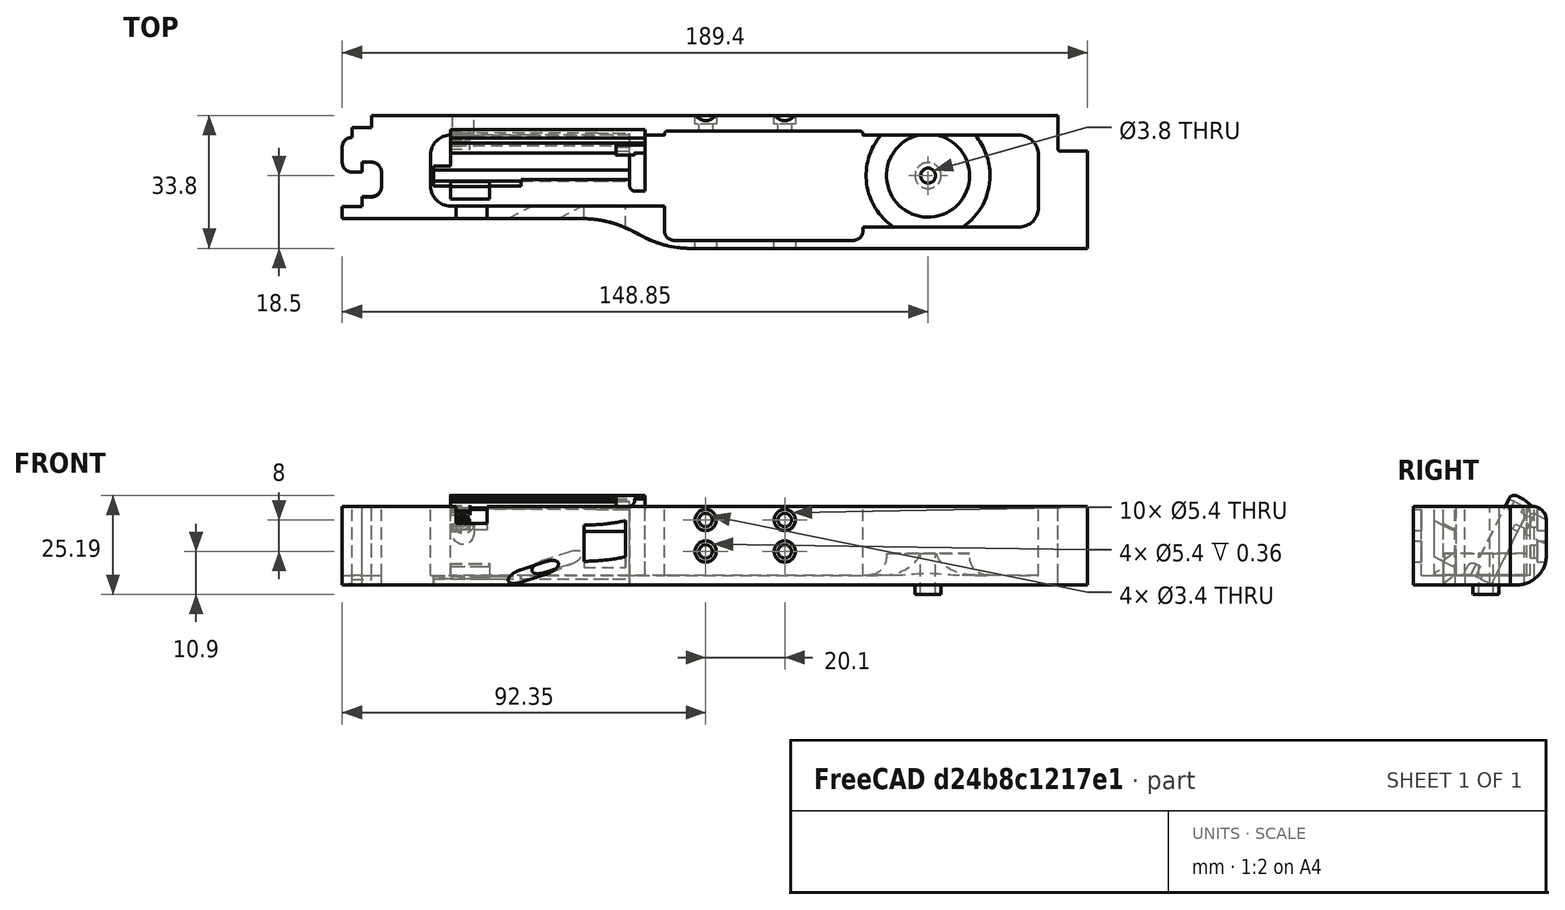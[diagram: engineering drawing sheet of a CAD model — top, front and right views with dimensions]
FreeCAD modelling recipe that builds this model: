
FCSTD DOCUMENT  (FreeCAD 0.19R0.19.2)
Label: v0_998
License: All rights reserved
LicenseURL: http://en.wikipedia.org/wiki/All_rights_reserved
objects: Sketcher::SketchObject×39, Part::Extrusion×31, Part::MultiFuse×19, Part::Cut×15, Part::Box×14, Part::Fillet×11, App::MeasureDistance×4, Part::Cylinder×4, Part::Revolution×1, Mesh::Feature×1
note: 134 computed .brp shape members not serialized (recipe doc carries the construction recipe); baked Part::Feature solids carry a one-line shape summary decoded from their .brp

FEATURE [Sketcher::SketchObject] Sketch
  FullyConstrained = true
  sketch-geometry (36):
    g0: LineSegment StartX=0 StartY=0 StartZ=0 EndX=154.4 EndY=0 EndZ=0
    g1: LineSegment StartX=154.4 StartY=0 StartZ=0 EndX=154.4 EndY=-7.6 EndZ=0
    g2: LineSegment StartX=32.5209 StartY=-26.2 StartZ=0 EndX=-7.5 EndY=-26.2 EndZ=0
    g3-g7: Circle x5 (B-spline internal-alignment scaffolding for g8; pole/knot coordinates omitted)
    g8: BSplineCurve PolesCount=5 KnotsCount=3 Degree=3 IsPeriodic=0
    g9: GeomPoint X=61.85 Y=-33.8 Z=0
    g10: GeomPoint X=47.185 Y=-29.9 Z=0
    g11: GeomPoint X=32.5209 Y=-26.2 Z=0
    g12: Circle CenterX=121.35 CenterY=-14.3 CenterZ=0 NormalX=0 NormalY=0 NormalZ=1 AngleXU=0 Radius=3.25
    g13: LineSegment StartX=-7.5 StartY=-26.2 StartZ=0 EndX=-27.5 EndY=-26.2 EndZ=0
    g14: LineSegment StartX=-20 StartY=0 StartZ=0 EndX=0 EndY=0 EndZ=0
    g15: LineSegment StartX=-25 StartY=-3.1 StartZ=0 EndX=-20 EndY=-3.1 EndZ=0
    g16: LineSegment StartX=-25 StartY=-3.1 StartZ=0 EndX=-25 EndY=-5.6 EndZ=0
    g17: LineSegment StartX=-27.5 StartY=-8.1 StartZ=0 EndX=-27.5 EndY=-11.85 EndZ=0
    g18: ArcOfCircle CenterX=-25 CenterY=-8.1 CenterZ=0 NormalX=0 NormalY=0 NormalZ=1 AngleXU=0 Radius=2.5 StartAngle=1.5708 EndAngle=3.14159
    g19: LineSegment StartX=-25 StartY=-14.35 StartZ=0 EndX=-22.5 EndY=-14.35 EndZ=0
    g20: ArcOfCircle CenterX=-25 CenterY=-11.85 CenterZ=0 NormalX=0 NormalY=0 NormalZ=1 AngleXU=0 Radius=2.5 StartAngle=3.14159 EndAngle=4.71239
    g21: LineSegment StartX=-22.5 StartY=-14.35 StartZ=0 EndX=-22.5 EndY=-11.85 EndZ=0
    g22: LineSegment StartX=-22.5 StartY=-11.85 StartZ=0 EndX=-20 EndY=-11.85 EndZ=0
    g23: ArcOfCircle CenterX=-20 CenterY=-14.35 CenterZ=0 NormalX=0 NormalY=0 NormalZ=1 AngleXU=0 Radius=2.5 StartAngle=8e-16 EndAngle=1.5708
    g24: LineSegment StartX=-17.5 StartY=-14.35 StartZ=0 EndX=-17.5 EndY=-18.1 EndZ=0
    g25: ArcOfCircle CenterX=-20 CenterY=-18.1 CenterZ=0 NormalX=0 NormalY=0 NormalZ=1 AngleXU=0 Radius=2.5 StartAngle=4.71239 EndAngle=6.28319
    g26: LineSegment StartX=-22.5 StartY=-20.6 StartZ=0 EndX=-20 EndY=-20.6 EndZ=0
    g27: LineSegment StartX=-22.5 StartY=-20.6 StartZ=0 EndX=-22.5 EndY=-23.1 EndZ=0
    g28: LineSegment StartX=-27.5 StartY=-23.1 StartZ=0 EndX=-22.5 EndY=-23.1 EndZ=0
    g29: LineSegment StartX=-20 StartY=-3.1 StartZ=0 EndX=-20 EndY=0 EndZ=0
    g30: LineSegment StartX=-27.5 StartY=-23.1 StartZ=0 EndX=-27.5 EndY=-26.2 EndZ=0
    g31: LineSegment StartX=154.4 StartY=-7.6 StartZ=0 EndX=154.4 EndY=-8.6 EndZ=0
    g32: ArcOfCircle CenterX=154.9 CenterY=-8.6 CenterZ=0 NormalX=0 NormalY=0 NormalZ=1 AngleXU=0 Radius=0.5 StartAngle=3.14159 EndAngle=4.71239
    g33: LineSegment StartX=154.9 StartY=-9.1 StartZ=0 EndX=161.9 EndY=-9.1 EndZ=0
    g34: LineSegment StartX=161.9 StartY=-9.1 StartZ=0 EndX=161.9 EndY=-33.8 EndZ=0
    g35: LineSegment StartX=161.9 StartY=-33.8 StartZ=0 EndX=61.85 EndY=-33.8 EndZ=0
  constraints (72):
    c: PointOnObject(g0,g-2)
    c: Horizontal(g0)
    c: Distance(g0) = 154.4
    c: DistanceY(g-1,g0) = 0
    c: Vertical(g1)
    c: Distance(g1) = 7.6
    c: Coincident(g1,g0)
    c: Horizontal(g2)
    c: Block(g2)
    c: Weight(g3) = 1
    c: Coincident(g8,g2)
    c: InternalAlignment(g3-g7 -> g8) x5
    c: InternalAlignment(g9,g8)
    c: InternalAlignment(g10,g8)
    c: InternalAlignment(g11,g8)
    c: Block(g12)
    c: Coincident(g13,g2)
    c: Horizontal(g13)
    c: Distance(g13) = 20
    c: Horizontal(g14)
    c: Distance(g14) = 20
    c: Coincident(g14,g0)
    c: Horizontal(g15)
    c: Vertical(g16)
    c: Coincident(g16,g15)
    c: Vertical(g17)
    c: Coincident(g18,g16)
    c: Block(g18)
    c: Coincident(g17,g18)
    c: Horizontal(g19)
    c: Coincident(g20,g17)
    c: Block(g20)
    c: Block(g19)
    c: Vertical(g21)
    c: Coincident(g21,g19)
    c: Horizontal(g22)
    c: Coincident(g22,g21)
    c: Coincident(g23,g22)
    c: Vertical(g24)
    c: Block(g23)
    c: Coincident(g24,g23)
    c: Coincident(g25,g24)
    c: Block(g25)
    c: Horizontal(g26)
    c: Coincident(g26,g25)
    c: Vertical(g27)
    c: Coincident(g27,g26)
    c: Horizontal(g28)
    c: Coincident(g28,g27)
    c: Block(g15)
    c: Block(g28)
    c: Coincident(g29,g15)
    c: Coincident(g29,g14)
    c: Vertical(g29)
    c: Coincident(g30,g28)
    c: Coincident(g30,g13)
    c: Vertical(g30)
    c: Vertical(g31)
    c: Distance(g31) = 1
    c: Coincident(g31,g1)
    c: Coincident(g32,g31)
    c: Block(g32)
    c: Coincident(g33,g32)
    c: Horizontal(g33)
    c: Coincident(g34,g33)
    c: Vertical(g34)
    c: Block(g34)
    c: Coincident(g35,g34)
    c: Horizontal(g35)
    c: Block(g35)
    c: Coincident(g8,g35)
    c: Block(g8)
FEATURE [Part::Extrusion] Extrude  label="mainBodyBaseExtrude"
  Base = -> Sketch
  Dir = (0,0,1)
  DirMode = 2
  FaceMakerClass = Part::FaceMakerBullseye
  LengthFwd = 2.4
  LengthRev = 0
  Solid = true
  Symmetric = false
FEATURE [Sketcher::SketchObject] Sketch001
  FullyConstrained = true
  sketch-geometry (75):
    g0: ArcOfCircle CenterX=144.4 CenterY=-10 CenterZ=0 NormalX=0 NormalY=0 NormalZ=1 AngleXU=0 Radius=5 StartAngle=4.345e-13 EndAngle=1.5708
    g1: LineSegment StartX=32.5209 StartY=-26.2 StartZ=0 EndX=-7.49911 EndY=-26.2 EndZ=0
    g2: LineSegment StartX=0 StartY=0 StartZ=0 EndX=154.4 EndY=0 EndZ=0
    g3-g7: Circle x5 (B-spline internal-alignment scaffolding for g8; pole/knot coordinates omitted)
    g8: BSplineCurve PolesCount=5 KnotsCount=3 Degree=3 IsPeriodic=0
    g9: GeomPoint X=61.85 Y=-33.8 Z=0
    g10: GeomPoint X=47.1857 Y=-29.9 Z=0
    g11: GeomPoint X=32.5209 Y=-26.2 Z=0
    g12: LineSegment StartX=154.4 StartY=0 StartZ=0 EndX=154.4 EndY=-7.6 EndZ=0
    g13: LineSegment StartX=20 StartY=-5 StartZ=0 EndX=54.35 EndY=-5 EndZ=0
    g14: LineSegment StartX=104.85 StartY=-5 StartZ=0 EndX=144.4 EndY=-5 EndZ=0
    g15: LineSegment StartX=54.35 StartY=-23 StartZ=0 EndX=20 EndY=-23 EndZ=0
    g16: LineSegment StartX=-27.4991 StartY=-26.2 StartZ=0 EndX=-7.49911 EndY=-26.2 EndZ=0
    g17: LineSegment StartX=-20 StartY=0 StartZ=0 EndX=0 EndY=0 EndZ=0
    g18: LineSegment StartX=-27.4991 StartY=-23.2 StartZ=0 EndX=-22.5 EndY=-23.2 EndZ=0
    g19: LineSegment StartX=-22.5 StartY=-20.7 StartZ=0 EndX=-22.5 EndY=-23.2 EndZ=0
    g20: LineSegment StartX=-22.5 StartY=-20.7 StartZ=0 EndX=-20 EndY=-20.7 EndZ=0
    g21: ArcOfCircle CenterX=-20 CenterY=-18.2 CenterZ=0 NormalX=0 NormalY=0 NormalZ=1 AngleXU=0 Radius=2.5 StartAngle=4.71239 EndAngle=6.28319
    g22: LineSegment StartX=-17.5 StartY=-14.4 StartZ=0 EndX=-17.5 EndY=-18.2 EndZ=0
    g23: ArcOfCircle CenterX=-20 CenterY=-14.4 CenterZ=0 NormalX=0 NormalY=0 NormalZ=1 AngleXU=0 Radius=2.5 StartAngle=9e-16 EndAngle=1.5708
    g24: LineSegment StartX=-22.5 StartY=-11.9 StartZ=0 EndX=-20 EndY=-11.9 EndZ=0
    g25: LineSegment StartX=-22.5 StartY=-14.4 StartZ=0 EndX=-22.5 EndY=-11.9 EndZ=0
    g26: LineSegment StartX=-25 StartY=-14.4 StartZ=0 EndX=-22.5 EndY=-14.4 EndZ=0
    g27: ArcOfCircle CenterX=-25 CenterY=-11.9 CenterZ=0 NormalX=0 NormalY=0 NormalZ=1 AngleXU=0 Radius=2.5 StartAngle=3.14159 EndAngle=4.71239
    g28: LineSegment StartX=-27.5 StartY=-8.1 StartZ=0 EndX=-27.5 EndY=-11.9 EndZ=0
    g29: ArcOfCircle CenterX=-25 CenterY=-8.1 CenterZ=0 NormalX=0 NormalY=0 NormalZ=1 AngleXU=0 Radius=2.5 StartAngle=1.5708 EndAngle=3.14159
    g30: LineSegment StartX=-25 StartY=-3.1 StartZ=0 EndX=-25 EndY=-5.6 EndZ=0
    g31: LineSegment StartX=-20 StartY=-3.1 StartZ=0 EndX=-25 EndY=-3.1 EndZ=0
    g32: LineSegment StartX=-20 StartY=0 StartZ=0 EndX=-20 EndY=-3.1 EndZ=0
    g33: LineSegment StartX=-27.4991 StartY=-26.2 StartZ=0 EndX=-27.4991 EndY=-23.2 EndZ=0
    g34: LineSegment StartX=4.09e-14 StartY=-5 StartZ=0 EndX=20 EndY=-5 EndZ=0
    g35: ArcOfCircle CenterX=7.1e-15 CenterY=-18 CenterZ=0 NormalX=0 NormalY=0 NormalZ=1 AngleXU=0 Radius=5 StartAngle=3.14159 EndAngle=4.71239
    g36: ArcOfCircle CenterX=4.26e-14 CenterY=-10 CenterZ=0 NormalX=0 NormalY=0 NormalZ=1 AngleXU=0 Radius=5 StartAngle=1.5708 EndAngle=3.14159
    g37: LineSegment StartX=-5 StartY=-18 StartZ=0 EndX=-5 EndY=-10 EndZ=0
    g38: LineSegment StartX=6.2e-15 StartY=-23 StartZ=0 EndX=20 EndY=-23 EndZ=0
    g39: LineSegment StartX=154.4 StartY=-7.6 StartZ=0 EndX=154.4 EndY=-8.6 EndZ=0
    g40: LineSegment StartX=154.9 StartY=-9.1 StartZ=0 EndX=161.9 EndY=-9.1 EndZ=0
    g41: ArcOfCircle CenterX=154.9 CenterY=-8.6 CenterZ=0 NormalX=0 NormalY=0 NormalZ=1 AngleXU=0 Radius=0.5 StartAngle=3.14159 EndAngle=4.71299
    g42: LineSegment StartX=104.85 StartY=-28.3916 StartZ=0 EndX=144.408 EndY=-28.3916 EndZ=0
    g43: LineSegment StartX=149.4 StartY=-10 StartZ=0 EndX=149.4 EndY=-23.4 EndZ=0
    g44: ArcOfCircle CenterX=144.408 CenterY=-23.4 CenterZ=0 NormalX=0 NormalY=0 NormalZ=1 AngleXU=0 Radius=4.99164 StartAngle=4.71239 EndAngle=6.28319
    g45: LineSegment StartX=104.85 StartY=-28.3916 StartZ=0 EndX=104.85 EndY=-28.7833 EndZ=0
    g46: LineSegment StartX=54.35 StartY=-28.7916 StartZ=0 EndX=54.35 EndY=-23 EndZ=0
    g47: LineSegment StartX=161.9 StartY=-33.8 StartZ=0 EndX=161.9 EndY=-9.1 EndZ=0
    g48: LineSegment StartX=61.85 StartY=-33.8 StartZ=0 EndX=161.9 EndY=-33.8 EndZ=0
    g49: Circle CenterX=54.35 CenterY=-28.7916 CenterZ=0 NormalX=0 NormalY=0 NormalZ=1 AngleXU=0 Radius=1
    g50: Circle CenterX=54.35 CenterY=-31.7916 CenterZ=0 NormalX=0 NormalY=0 NormalZ=1 AngleXU=0 Radius=1
    g51: Circle CenterX=57.35 CenterY=-31.7916 CenterZ=0 NormalX=0 NormalY=0 NormalZ=1 AngleXU=0 Radius=1
    g52: BSplineCurve PolesCount=3 KnotsCount=2 Degree=2 IsPeriodic=0
    g53: GeomPoint X=54.35 Y=-28.7916 Z=0
    g54: GeomPoint X=57.35 Y=-31.7916 Z=0
    g55: Circle CenterX=104.85 CenterY=-28.7833 CenterZ=0 NormalX=0 NormalY=0 NormalZ=1 AngleXU=0 Radius=1
    g56: Circle CenterX=104.85 CenterY=-31.7916 CenterZ=0 NormalX=0 NormalY=0 NormalZ=1 AngleXU=0 Radius=1
    g57: Circle CenterX=101.85 CenterY=-31.7916 CenterZ=0 NormalX=0 NormalY=0 NormalZ=1 AngleXU=0 Radius=1
    g58: BSplineCurve PolesCount=3 KnotsCount=2 Degree=2 IsPeriodic=0
    g59: GeomPoint X=104.85 Y=-28.7833 Z=0
    g60: GeomPoint X=101.85 Y=-31.7916 Z=0
    g61: LineSegment StartX=57.35 StartY=-31.7916 StartZ=0 EndX=101.85 EndY=-31.7916 EndZ=0
    g62: Circle CenterX=54.35 CenterY=-5 CenterZ=0 NormalX=0 NormalY=0 NormalZ=1 AngleXU=0 Radius=1
    g63: Circle CenterX=54.35 CenterY=-4 CenterZ=0 NormalX=0 NormalY=0 NormalZ=1 AngleXU=0 Radius=1
    g64: Circle CenterX=55.15 CenterY=-4 CenterZ=0 NormalX=0 NormalY=0 NormalZ=1 AngleXU=0 Radius=1
    g65: BSplineCurve PolesCount=3 KnotsCount=2 Degree=2 IsPeriodic=0
    g66: GeomPoint X=54.35 Y=-5 Z=0
    g67: GeomPoint X=55.15 Y=-4 Z=0
    g68: Circle CenterX=104.85 CenterY=-5 CenterZ=0 NormalX=0 NormalY=0 NormalZ=1 AngleXU=0 Radius=1
    g69: Circle CenterX=104.85 CenterY=-4 CenterZ=0 NormalX=0 NormalY=0 NormalZ=1 AngleXU=0 Radius=1
    g70: Circle CenterX=104.05 CenterY=-4 CenterZ=0 NormalX=0 NormalY=0 NormalZ=1 AngleXU=0 Radius=1
    g71: BSplineCurve PolesCount=3 KnotsCount=2 Degree=2 IsPeriodic=0
    g72: GeomPoint X=104.85 Y=-5 Z=0
    g73: GeomPoint X=104.05 Y=-4 Z=0
    g74: LineSegment StartX=104.05 StartY=-4 StartZ=0 EndX=55.15 EndY=-4 EndZ=0
  constraints (156):
    c: PointOnObject(g2,g-2)
    c: DistanceY(g-1,g2) = 0
    c: Block(g0)
    c: Horizontal(g1)
    c: Distance(g1) = 40.02
    c: Horizontal(g2)
    c: Block(g2)
    c: Weight(g3) = 1
    c: Equal(g3, g4-g7) x4
    c: Coincident(g8,g1)
    c: InternalAlignment(g3-g7 -> g8) x5
    c: InternalAlignment(g9,g8)
    c: InternalAlignment(g10,g8)
    c: InternalAlignment(g11,g8)
    c: Vertical(g12)
    c: Coincident(g12,g2)
    c: Distance(g12) = 7.6
    c: Block(g12)
    c: Horizontal(g13)
    c: Coincident(g14,g0)
    c: Horizontal(g14)
    c: Horizontal(g15)
    c: Horizontal(g16)
    c: Distance(g16) = 20
    c: Coincident(g1,g16)
    c: Horizontal(g17)
    c: Distance(g17) = 20
    c: Coincident(g17,g2)
    c: Horizontal(g31)
    c: Vertical(g30)
    c: Coincident(g29,g30)
    c: Vertical(g28)
    c: Block(g29)
    c: Coincident(g27,g28)
    c: Block(g27)
    c: Horizontal(g26)
    c: Coincident(g26,g27)
    c: Vertical(g25)
    c: Coincident(g25,g26)
    c: Horizontal(g24)
    c: Coincident(g23,g24)
    c: Block(g23)
    c: Vertical(g22)
    c: Coincident(g21,g22)
    c: Block(g21)
    c: Horizontal(g20)
    c: Coincident(g20,g21)
    c: Vertical(g19)
    c: Coincident(g19,g20)
    c: Horizontal(g18)
    c: Coincident(g18,g19)
    c: Coincident(g32,g17)
    c: Coincident(g32,g31)
    c: Vertical(g32)
    c: Coincident(g33,g16)
    c: Coincident(g33,g18)
    c: Vertical(g33)
    c: Block(g33)
    c: Block(g18)
    c: Block(g22)
    c: Block(g26)
    c: Block(g25)
    c: Block(g24)
    c: Block(g28)
    c: Block(g31)
    c: Block(g30)
    c: Horizontal(g34)
    c: Distance(g34) = 20
    c: Block(g35)
    c: Block(g36)
    c: Coincident(g37,g35)
    c: Coincident(g37,g36)
    c: Vertical(g37)
    c: Coincident(g38,g35)
    c: Coincident(g38,g15)
    c: Horizontal(g38)
    c: Block(g38)
    c: Block(g34)
    c: Block(g13)
    c: Vertical(g39)
    c: Distance(g39) = 1
    c: Coincident(g39,g12)
    c: Horizontal(g40)
    c: Coincident(g41,g39)
    c: Coincident(g41,g40)
    c: Block(g39)
    c: Block(g41)
    c: Horizontal(g42)
    c: Vertical(g43)
    c: Distance(g43) = 13.4
    c: Coincident(g43,g0)
    c: Block(g42)
    c: Block(g43)
    c: Coincident(g44,g43)
    c: Coincident(g44,g42)
    c: Block(g44)
    c: Distance(g15) = 34.35
    c: Coincident(g45,g42)
    c: Vertical(g45)
    c: Coincident(g46,g15)
    c: Vertical(g46)
    c: Coincident(g47,g40)
    c: Vertical(g47)
    c: Block(g47)
    c: Coincident(g48,g47)
    c: Horizontal(g48)
    c: Block(g48)
    c: Coincident(g8,g48)
    c: Block(g8)
    c: Coincident(g52,g46)
    c: Weight(g49) = 1
    c: Equal(g49,g50)
    c: Equal(g49,g51)
    c: InternalAlignment(g49,g52)
    c: InternalAlignment(g50,g52)
    c: InternalAlignment(g51,g52)
    c: InternalAlignment(g53,g52)
    c: InternalAlignment(g54,g52)
    c: Coincident(g58,g45)
    c: Weight(g55) = 1
    c: Equal(g55,g56)
    c: Equal(g55,g57)
    c: InternalAlignment(g55,g58)
    c: InternalAlignment(g56,g58)
    c: InternalAlignment(g57,g58)
    c: InternalAlignment(g59,g58)
    c: InternalAlignment(g60,g58)
    c: Block(g58)
    c: Block(g52)
    c: Coincident(g61,g52)
    c: Coincident(g61,g58)
    c: Horizontal(g61)
    c: Block(g14)
    c: Coincident(g65,g13)
    c: Weight(g62) = 1
    c: Equal(g62,g63)
    c: Equal(g62,g64)
    c: InternalAlignment(g62,g65)
    c: InternalAlignment(g63,g65)
    c: InternalAlignment(g64,g65)
    c: InternalAlignment(g66,g65)
    c: InternalAlignment(g67,g65)
    c: Block(g65)
    c: Coincident(g71,g14)
    c: Weight(g68) = 1
    c: Equal(g68,g69)
    c: Equal(g68,g70)
    c: InternalAlignment(g68,g71)
    c: InternalAlignment(g69,g71)
    c: InternalAlignment(g70,g71)
    c: InternalAlignment(g72,g71)
    c: InternalAlignment(g73,g71)
    c: Block(g71)
    c: Coincident(g74,g71)
    c: Coincident(g74,g65)
    c: Horizontal(g74)
FEATURE [Sketcher::SketchObject] Sketch005
  FullyConstrained = true
  Placement = pos=(0,0,0) rot=(1,0,0;1.5708rad)
  sketch-geometry (4):
    g0: Circle CenterX=84.95 CenterY=16.5 CenterZ=0 NormalX=0 NormalY=0 NormalZ=1 AngleXU=0 Radius=1.7
    g1: Circle CenterX=84.95 CenterY=8.5 CenterZ=0 NormalX=0 NormalY=0 NormalZ=1 AngleXU=0 Radius=1.7
    g2: Circle CenterX=64.85 CenterY=8.5 CenterZ=0 NormalX=0 NormalY=0 NormalZ=1 AngleXU=0 Radius=1.7
    g3: Circle CenterX=64.85 CenterY=16.5 CenterZ=0 NormalX=0 NormalY=0 NormalZ=1 AngleXU=0 Radius=1.7
  constraints (4):
    c: Block(g0)
    c: Block(g1)
    c: Block(g2)
    c: Block(g3)
FEATURE [Part::Extrusion] Extrude004  label="removeFromMainBodyToCreateScrewHolesForSolenoidExtrude004"
  Base = -> Sketch005
  Dir = (0,-1,1.1e-15)
  DirMode = 2
  FaceMakerClass = Part::FaceMakerBullseye
  LengthFwd = 10
  LengthRev = 0
  Solid = true
  Symmetric = false
FEATURE [Sketcher::SketchObject] Sketch004
  FullyConstrained = true
  Placement = pos=(0,0,0) rot=(1,0,0;1.5708rad)
  sketch-geometry (12):
    g0: LineSegment StartX=15.75 StartY=2.5 StartZ=0 EndX=15.75 EndY=0 EndZ=0
    g1: Circle CenterX=15.75 CenterY=2.5 CenterZ=0 NormalX=0 NormalY=0 NormalZ=1 AngleXU=0 Radius=1
    g2: Circle CenterX=10.55 CenterY=2.5 CenterZ=0 NormalX=0 NormalY=0 NormalZ=1 AngleXU=0 Radius=1
    g3: Circle CenterX=10.55 CenterY=8 CenterZ=0 NormalX=0 NormalY=0 NormalZ=1 AngleXU=0 Radius=1
    g4: BSplineCurve PolesCount=3 KnotsCount=2 Degree=2 IsPeriodic=0
    g5: GeomPoint X=15.75 Y=2.5 Z=0
    g6: GeomPoint X=10.55 Y=8 Z=0
    g7: LineSegment StartX=1.9 StartY=8 StartZ=0 EndX=10.55 EndY=8 EndZ=0
    g8: LineSegment StartX=1.9 StartY=-2.4 StartZ=0 EndX=1.9 EndY=8 EndZ=0
    g9: LineSegment StartX=3.30092 StartY=-2.4 StartZ=0 EndX=3.30092 EndY=0 EndZ=0
    g10: LineSegment StartX=15.75 StartY=0 StartZ=0 EndX=3.30092 EndY=0 EndZ=0
    g11: LineSegment StartX=3.30092 StartY=-2.4 StartZ=0 EndX=1.9 EndY=-2.4 EndZ=0
  constraints (26):
    c: Vertical(g0)
    c: Distance(g0) = 2.5
    c: Coincident(g4,g0)
    c: Weight(g1) = 1
    c: Equal(g1,g2)
    c: Equal(g1,g3)
    c: InternalAlignment(g1,g4)
    c: InternalAlignment(g2,g4)
    c: InternalAlignment(g3,g4)
    c: InternalAlignment(g5,g4)
    c: InternalAlignment(g6,g4)
    c: Block(g4)
    c: Coincident(g7,g4)
    c: Horizontal(g7)
    c: Vertical(g8)
    c: Coincident(g8,g7)
    c: Block(g8)
    c: Vertical(g9)
    c: Coincident(g10,g0)
    c: PointOnObject(g10,g-1)
    c: Horizontal(g10)
    c: Coincident(g10,g9)
    c: Block(g9)
    c: Coincident(g11,g9)
    c: Coincident(g11,g8)
    c: Horizontal(g11)
FEATURE [Sketcher::SketchObject] Sketch007
  FullyConstrained = true
  Placement = pos=(0,-14.3,2.37) rot=(-1,0,0;2.03453rad)
  sketch-geometry (6):
    g0: LineSegment StartX=0 StartY=0 StartZ=0 EndX=45.5 EndY=0 EndZ=0
    g1: LineSegment StartX=0 StartY=0 StartZ=0 EndX=0 EndY=-21.2 EndZ=0
    g2: LineSegment StartX=45.5 StartY=0 StartZ=0 EndX=49.5 EndY=0 EndZ=0
    g3: LineSegment StartX=49.5 StartY=0 StartZ=0 EndX=49.5 EndY=-21.2 EndZ=0
    g4: LineSegment StartX=49.5 StartY=-21.2 StartZ=0 EndX=0 EndY=-21.2 EndZ=0
    g5: Circle CenterX=3.25 CenterY=-18.05 CenterZ=0 NormalX=0 NormalY=0 NormalZ=1 AngleXU=0 Radius=1.6
  constraints (15):
    c: Coincident(g0,g-1)
    c: Horizontal(g0)
    c: Distance(g0) = 45.5
    c: Coincident(g1,g0)
    c: Vertical(g1)
    c: Horizontal(g2)
    c: Distance(g2) = 4
    c: Coincident(g2,g0)
    c: Coincident(g3,g2)
    c: Vertical(g3)
    c: Block(g3)
    c: Coincident(g4,g3)
    c: Horizontal(g4)
    c: Coincident(g4,g1)
    c: Block(g5)
FEATURE [Part::Extrusion] Extrude005  label="solenoidDriverHolderExtrude005"
  Base = -> Sketch007
  Dir = (0,0.894389,-0.447291)
  DirMode = 2
  FaceMakerClass = Part::FaceMakerBullseye
  LengthFwd = 10
  LengthRev = 0
  Placement = pos=(0,0,-2) rot=(0,0,1;0rad)
  Solid = true
  Symmetric = false
FEATURE [Sketcher::SketchObject] Sketch008
  FullyConstrained = false
  Placement = pos=(0,-4.3,-2.6) rot=(-1,0,0;2.03453rad)
  sketch-geometry (1):
    g0: Circle CenterX=42.25 CenterY=-3.15 CenterZ=0 NormalX=0 NormalY=0 NormalZ=1 AngleXU=0 Radius=4.5
FEATURE [Sketcher::SketchObject] Sketch009
  FullyConstrained = true
  Placement = pos=(0,-4.3,-2.6) rot=(-1,0,0;2.03453rad)
  sketch-geometry (1):
    g0: Circle CenterX=3.25 CenterY=-18.0217 CenterZ=0 NormalX=0 NormalY=0 NormalZ=1 AngleXU=0 Radius=2.8
  constraints (1):
    c: Block(g0)
FEATURE [Sketcher::SketchObject] Sketch010
  FullyConstrained = true
  Placement = pos=(0,-14.3,2.37) rot=(-1,0,0;2.03453rad)
  sketch-geometry (1):
    g0: Circle CenterX=3.25 CenterY=-18.05 CenterZ=0 NormalX=0 NormalY=0 NormalZ=1 AngleXU=0 Radius=1.6
  constraints (1):
    c: Block(g0)
FEATURE [Part::Extrusion] Extrude008  label="removeFromScrewHole3"
  Base = -> Sketch010
  Dir = (0,0.894389,-0.447291)
  DirMode = 2
  FaceMakerClass = Part::FaceMakerBullseye
  LengthFwd = -25
  LengthRev = 0
  Placement = pos=(0,4,-4) rot=(0,0,1;0rad)
  Solid = true
  Symmetric = false
FEATURE [Sketcher::SketchObject] Sketch011
  FullyConstrained = true
  Placement = pos=(0,-14.3,2.37) rot=(-1,0,0;2.03453rad)
  sketch-geometry (4):
    g0: LineSegment StartX=49.5 StartY=-21.2 StartZ=0 EndX=49.5 EndY=-22.8 EndZ=0
    g1: LineSegment StartX=49.5 StartY=-22.8 StartZ=0 EndX=0.002238 EndY=-22.8 EndZ=0
    g2: LineSegment StartX=0.002238 StartY=-21.2 StartZ=0 EndX=0.002238 EndY=-22.8 EndZ=0
    g3: LineSegment StartX=49.5 StartY=-21.2 StartZ=0 EndX=0.002238 EndY=-21.2 EndZ=0
  constraints (10):
    c: Vertical(g0)
    c: Distance(g0) = 1.6
    c: Coincident(g1,g0)
    c: Horizontal(g1)
    c: Vertical(g2)
    c: Coincident(g2,g1)
    c: Coincident(g3,g0)
    c: Coincident(g3,g2)
    c: Horizontal(g3)
    c: Block(g3)
FEATURE [Part::Extrusion] Extrude009  label="solenoidDriverTopLipFront"
  Base = -> Sketch011
  Dir = (0,0.894389,-0.447291)
  DirMode = 2
  FaceMakerClass = Part::FaceMakerBullseye
  LengthFwd = -2
  LengthRev = 0
  Placement = pos=(0,-2.9,-0.35) rot=(0,0,1;0rad)
  Solid = true
  Symmetric = false
FEATURE [Sketcher::SketchObject] Sketch012
  FullyConstrained = true
  Placement = pos=(0,-14.3,2.37) rot=(-1,0,0;2.03453rad)
  sketch-geometry (4):
    g0: LineSegment StartX=49.5 StartY=-21.2 StartZ=0 EndX=49.5 EndY=-22.8 EndZ=0
    g1: LineSegment StartX=49.5 StartY=-22.8 StartZ=0 EndX=0.002238 EndY=-22.8 EndZ=0
    g2: LineSegment StartX=0.002238 StartY=-21.2 StartZ=0 EndX=0.002238 EndY=-22.8 EndZ=0
    g3: LineSegment StartX=49.5 StartY=-21.2 StartZ=0 EndX=0.002238 EndY=-21.2 EndZ=0
  constraints (10):
    c: Vertical(g0)
    c: Distance(g0) = 1.6
    c: Coincident(g1,g0)
    c: Horizontal(g1)
    c: Vertical(g2)
    c: Coincident(g2,g1)
    c: Coincident(g3,g0)
    c: Coincident(g3,g2)
    c: Horizontal(g3)
    c: Block(g3)
FEATURE [Part::Extrusion] Extrude010  label="solenoidDriverTopLipLowerExtrude010"
  Base = -> Sketch012
  Dir = (0,0.894389,-0.447291)
  DirMode = 2
  FaceMakerClass = Part::FaceMakerBullseye
  LengthFwd = 5.05
  LengthRev = 0
  Solid = true
  Symmetric = false
FEATURE [Sketcher::SketchObject] Sketch015
  FullyConstrained = true
  Placement = pos=(0,-14.3,2.37) rot=(-1,0,0;2.03453rad)
  sketch-geometry (4):
    g0: LineSegment StartX=0 StartY=1.5 StartZ=0 EndX=0 EndY=0 EndZ=0
    g1: LineSegment StartX=0 StartY=1.5 StartZ=0 EndX=5 EndY=1.5 EndZ=0
    g2: LineSegment StartX=5 StartY=1.5 StartZ=0 EndX=5 EndY=0 EndZ=0
    g3: LineSegment StartX=0 StartY=0 StartZ=0 EndX=5 EndY=0 EndZ=0
  constraints (13):
    c: Vertical(g0)
    c: Distance(g0) = 1.5
    c: Horizontal(g1)
    c: Distance(g1) = 5
    c: Coincident(g1,g0)
    c: Vertical(g2)
    c: Distance(g2) = 1.5
    c: Coincident(g2,g1)
    c: Block(g1)
    c: Block(g2)
    c: Block(g0)
    c: Coincident(g3,g0)
    c: Coincident(g3,g2)
FEATURE [Part::Extrusion] Extrude013  label="solenoidDriverBottomLipTopExtrude012"
  Base = -> Sketch015
  Dir = (0,0.894389,-0.447291)
  DirMode = 2
  FaceMakerClass = Part::FaceMakerBullseye
  LengthFwd = -6.5
  LengthRev = 0
  Placement = pos=(0,-14.15,19.65) rot=(1,0,0;1.5708rad)
  Solid = true
  Symmetric = false
FEATURE [Sketcher::SketchObject] Sketch016
  FullyConstrained = true
  Placement = pos=(0,0,0) rot=(1,0,0;1.5708rad)
  sketch-geometry (4):
    g0: Circle CenterX=84.15 CenterY=16.5 CenterZ=0 NormalX=0 NormalY=0 NormalZ=1 AngleXU=0 Radius=2.7
    g1: Circle CenterX=64.05 CenterY=16.5 CenterZ=0 NormalX=0 NormalY=0 NormalZ=1 AngleXU=0 Radius=2.7
    g2: Circle CenterX=64.05 CenterY=8.5 CenterZ=0 NormalX=0 NormalY=0 NormalZ=1 AngleXU=0 Radius=2.7
    g3: Circle CenterX=84.15 CenterY=8.5 CenterZ=0 NormalX=0 NormalY=0 NormalZ=1 AngleXU=0 Radius=2.7
  constraints (4):
    c: Block(g0)
    c: Block(g1)
    c: Block(g3)
    c: Block(g2)
FEATURE [Part::Extrusion] Extrude014  label="removeFromMainBodyToCreateScrewHoleCounterSinks"
  Base = -> Sketch016
  Dir = (0,-1,1.1e-15)
  DirMode = 2
  FaceMakerClass = Part::FaceMakerBullseye
  LengthFwd = 1.9
  LengthRev = 0
  Placement = pos=(0.8,-0.36,0) rot=(0,0,1;0rad)
  Solid = true
  Symmetric = false
FEATURE [Part::Extrusion] Extrude015  label="removeFromScrewHole2Extrude007"
  Base = -> Sketch009
  Dir = (0,0.894389,-0.447291)
  DirMode = 2
  FaceMakerClass = Part::FaceMakerBullseye
  LengthFwd = 10
  LengthRev = 0
  Placement = pos=(0,-8,2) rot=(0,0,1;0rad)
  Solid = true
  Symmetric = false
FEATURE [Sketcher::SketchObject] Sketch017
  FullyConstrained = true
  Placement = pos=(0,-14.3,2.37) rot=(-1,0,0;2.03453rad)
  sketch-geometry (4):
    g0: LineSegment StartX=0 StartY=1.5 StartZ=0 EndX=0 EndY=0 EndZ=0
    g1: LineSegment StartX=0 StartY=1.5 StartZ=0 EndX=5 EndY=1.5 EndZ=0
    g2: LineSegment StartX=5 StartY=1.5 StartZ=0 EndX=5 EndY=0 EndZ=0
    g3: LineSegment StartX=0 StartY=0 StartZ=0 EndX=5 EndY=0 EndZ=0
  constraints (13):
    c: Vertical(g0)
    c: Distance(g0) = 1.5
    c: Horizontal(g1)
    c: Distance(g1) = 5
    c: Coincident(g1,g0)
    c: Vertical(g2)
    c: Distance(g2) = 1.5
    c: Coincident(g2,g1)
    c: Block(g1)
    c: Block(g2)
    c: Block(g0)
    c: Coincident(g3,g0)
    c: Coincident(g3,g2)
FEATURE [Part::Extrusion] Extrude016  label="solenoidDriverBottomLipTopExtrude013"
  Base = -> Sketch017
  Dir = (0,0.894389,-0.447291)
  DirMode = 2
  FaceMakerClass = Part::FaceMakerBullseye
  LengthFwd = -6.5
  LengthRev = 0
  Placement = pos=(0,-15.45,20.3) rot=(1,0,0;1.5708rad)
  Solid = true
  Symmetric = false
FEATURE [Part::Fillet] Fillet005  label="solenoidDriverBottomLipTopFillet005"
  Base = -> Extrude016
  Edges = 1 edges r=1.4: [Edge6]
FEATURE [Sketcher::SketchObject] Sketch018
  FullyConstrained = true
  Placement = pos=(38.5,-14.3,2.37) rot=(-1,0,0;2.03453rad)
  sketch-geometry (4):
    g0: LineSegment StartX=11 StartY=0 StartZ=0 EndX=11 EndY=1.5 EndZ=0
    g1: LineSegment StartX=11 StartY=0 StartZ=0 EndX=3.6 EndY=0 EndZ=0
    g2: LineSegment StartX=3.6 StartY=0 StartZ=0 EndX=3.6 EndY=1.5 EndZ=0
    g3: LineSegment StartX=11 StartY=1.5 StartZ=0 EndX=3.6 EndY=1.5 EndZ=0
  constraints (12):
    c: PointOnObject(g0,g-1)
    c: Vertical(g0)
    c: Distance(g0) = 1.5
    c: Horizontal(g1)
    c: Distance(g1) = 7.4
    c: Coincident(g1,g0)
    c: Block(g0)
    c: Coincident(g2,g1)
    c: Vertical(g2)
    c: Coincident(g3,g0)
    c: Horizontal(g3)
    c: Coincident(g2,g3)
FEATURE [Part::Extrusion] Extrude017
  Base = -> Sketch018
  Dir = (0,0.894389,-0.447291)
  DirMode = 2
  FaceMakerClass = Part::FaceMakerBullseye
  LengthFwd = 4
  LengthRev = 0
  Placement = pos=(0,-8.212,34.025) rot=(1,0,0;1.5708rad)
  Solid = true
  Symmetric = false
FEATURE [Sketcher::SketchObject] Sketch019
  FullyConstrained = true
  Placement = pos=(0,0,0) rot=(1,0,0;1.5708rad)
  sketch-geometry (4):
    g0: Circle CenterX=84.95 CenterY=8.5 CenterZ=0 NormalX=0 NormalY=0 NormalZ=1 AngleXU=0 Radius=2.7
    g1: Circle CenterX=64.85 CenterY=8.5 CenterZ=0 NormalX=0 NormalY=0 NormalZ=1 AngleXU=0 Radius=2.7
    g2: Circle CenterX=64.85 CenterY=16.5 CenterZ=0 NormalX=0 NormalY=0 NormalZ=1 AngleXU=0 Radius=2.7
    g3: Circle CenterX=84.95 CenterY=16.5 CenterZ=0 NormalX=0 NormalY=0 NormalZ=1 AngleXU=0 Radius=2.7
  constraints (4):
    c: Block(g3)
    c: Block(g2)
    c: Block(g0)
    c: Block(g1)
FEATURE [Part::Extrusion] Extrude019  label="removeSolenoidAdjusterHoles"
  Base = -> Sketch019
  Dir = (0,-1,1.1e-15)
  DirMode = 2
  FaceMakerClass = Part::FaceMakerBullseye
  LengthFwd = 6
  LengthRev = 0
  Placement = pos=(0,-30,0) rot=(0,0,1;0rad)
  Solid = true
  Symmetric = false
FEATURE [Sketcher::SketchObject] Sketch020
  FullyConstrained = true
  Placement = pos=(0,-14.3,2.37) rot=(-1,0,0;2.03453rad)
  sketch-geometry (6):
    g0: LineSegment StartX=45.5 StartY=-21.2 StartZ=0 EndX=49.5 EndY=-21.2 EndZ=0
    g1: LineSegment StartX=45.5 StartY=0 StartZ=0 EndX=49.5 EndY=0 EndZ=0
    g2: LineSegment StartX=49.5 StartY=0 StartZ=0 EndX=49.5 EndY=-21.2 EndZ=0
    g3: LineSegment StartX=4 StartY=0 StartZ=0 EndX=4 EndY=-21.2 EndZ=0
    g4: LineSegment StartX=45.5 StartY=-21.2 StartZ=0 EndX=4 EndY=-21.2 EndZ=0
    g5: LineSegment StartX=4 StartY=0 StartZ=0 EndX=45.5 EndY=0 EndZ=0
  constraints (16):
    c: Horizontal(g0)
    c: Distance(g0) = 4
    c: Horizontal(g1)
    c: Distance(g1) = 4
    c: Coincident(g2,g1)
    c: Coincident(g2,g0)
    c: Vertical(g2)
    c: Block(g2)
    c: Vertical(g3)
    c: Coincident(g4,g0)
    c: Horizontal(g4)
    c: Coincident(g4,g3)
    c: Coincident(g5,g1)
    c: Horizontal(g5)
    c: Block(g3)
    c: Block(g5)
FEATURE [Part::Box] Box  label="Cube"
  AttacherType = Attacher::AttachEngine3D
  Height = 10
  Length = 190
  Placement = pos=(-30,0,0) rot=(0,0,1;0rad)
  Width = 10
FEATURE [Part::Fillet] Fillet008
  Base = -> Box
  Edges = 1 edges r=7.5: [Edge11]
FEATURE [Part::Box] Box001  label="Cube001"
  AttacherType = Attacher::AttachEngine3D
  Height = 10
  Length = 190
  Placement = pos=(-35,0,0) rot=(0,0,1;0rad)
  Width = 10
FEATURE [Part::Cut] Cut  label="filletMain"
  Base = -> Box001
  Placement = pos=(0,-10,0) rot=(0,0,1;0rad)
  Tool = -> Fillet008
FEATURE [Part::Box] Box002  label="Cube002"
  AttacherType = Attacher::AttachEngine3D
  Height = 30
  Length = 190
  Placement = pos=(-20,0,0) rot=(0,0,1;0rad)
  Width = 10
FEATURE [Part::Box] Box003  label="Cube003"
  AttacherType = Attacher::AttachEngine3D
  Height = 10
  Length = 190
  Placement = pos=(-90,-50,-10) rot=(0,0,1;0rad)
  Width = 50
FEATURE [Sketcher::SketchObject] Sketch021
  FullyConstrained = true
  Placement = pos=(0,-14.3,2.37) rot=(-1,0,0;2.03453rad)
  sketch-geometry (6):
    g0: LineSegment StartX=41.65 StartY=-3.15 StartZ=0 EndX=38.95 EndY=-3.15 EndZ=0
    g1: LineSegment StartX=36.25 StartY=-3.15 StartZ=0 EndX=38.95 EndY=-3.15 EndZ=0
    g2: LineSegment StartX=41.65 StartY=-3.15 StartZ=0 EndX=41.65 EndY=-7.15 EndZ=0
    g3: LineSegment StartX=38.95 StartY=-7.15 StartZ=0 EndX=41.65 EndY=-7.15 EndZ=0
    g4: LineSegment StartX=38.95 StartY=-7.15 StartZ=0 EndX=36.25 EndY=-7.15 EndZ=0
    g5: LineSegment StartX=36.25 StartY=-3.15 StartZ=0 EndX=36.25 EndY=-7.15 EndZ=0
  constraints (16):
    c: Horizontal(g0)
    c: Distance(g0) = 2.7
    c: Horizontal(g1)
    c: Distance(g1) = 2.7
    c: Coincident(g1,g0)
    c: Block(g0)
    c: Coincident(g2,g0)
    c: Vertical(g2)
    c: Horizontal(g3)
    c: Coincident(g3,g2)
    c: Horizontal(g4)
    c: Coincident(g5,g1)
    c: Vertical(g5)
    c: Coincident(g5,g4)
    c: Block(g3)
    c: Block(g4)
FEATURE [Sketcher::SketchObject] Sketch022
  FullyConstrained = true
  Placement = pos=(0,-14.3,2.37) rot=(-1,0,0;2.03453rad)
  sketch-geometry (6):
    g0: LineSegment StartX=41.65 StartY=-3.15 StartZ=0 EndX=38.95 EndY=-3.15 EndZ=0
    g1: LineSegment StartX=36.25 StartY=-3.15 StartZ=0 EndX=38.95 EndY=-3.15 EndZ=0
    g2: LineSegment StartX=41.65 StartY=-3.15 StartZ=0 EndX=41.65 EndY=-7.15 EndZ=0
    g3: LineSegment StartX=38.95 StartY=-7.15 StartZ=0 EndX=41.65 EndY=-7.15 EndZ=0
    g4: LineSegment StartX=38.95 StartY=-7.15 StartZ=0 EndX=36.25 EndY=-7.15 EndZ=0
    g5: LineSegment StartX=36.25 StartY=-3.15 StartZ=0 EndX=36.25 EndY=-7.15 EndZ=0
  constraints (16):
    c: Horizontal(g0)
    c: Distance(g0) = 2.7
    c: Horizontal(g1)
    c: Distance(g1) = 2.7
    c: Coincident(g1,g0)
    c: Block(g0)
    c: Coincident(g2,g0)
    c: Vertical(g2)
    c: Horizontal(g3)
    c: Coincident(g3,g2)
    c: Horizontal(g4)
    c: Coincident(g5,g1)
    c: Vertical(g5)
    c: Coincident(g5,g4)
    c: Block(g3)
    c: Block(g4)
FEATURE [Sketcher::SketchObject] Sketch024
  FullyConstrained = true
  Placement = pos=(0,-14.3,2.37) rot=(-1,0,0;2.03453rad)
  sketch-geometry (4):
    g0: LineSegment StartX=49.5 StartY=-21.2 StartZ=0 EndX=49.5 EndY=-22.8 EndZ=0
    g1: LineSegment StartX=49.5 StartY=-22.8 StartZ=0 EndX=0.002238 EndY=-22.8 EndZ=0
    g2: LineSegment StartX=0.002238 StartY=-21.2 StartZ=0 EndX=0.002238 EndY=-22.8 EndZ=0
    g3: LineSegment StartX=49.5 StartY=-21.2 StartZ=0 EndX=0.002238 EndY=-21.2 EndZ=0
  constraints (10):
    c: Vertical(g0)
    c: Distance(g0) = 1.6
    c: Coincident(g1,g0)
    c: Horizontal(g1)
    c: Vertical(g2)
    c: Coincident(g2,g1)
    c: Coincident(g3,g0)
    c: Coincident(g3,g2)
    c: Horizontal(g3)
    c: Block(g3)
FEATURE [Sketcher::SketchObject] Sketch025
  FullyConstrained = true
  Placement = pos=(0,-14.3,2.37) rot=(-1,0,0;2.03453rad)
  sketch-geometry (4):
    g0: LineSegment StartX=0 StartY=1.5 StartZ=0 EndX=0 EndY=0 EndZ=0
    g1: LineSegment StartX=0 StartY=1.5 StartZ=0 EndX=5 EndY=1.5 EndZ=0
    g2: LineSegment StartX=5 StartY=1.5 StartZ=0 EndX=5 EndY=0 EndZ=0
    g3: LineSegment StartX=0 StartY=0 StartZ=0 EndX=5 EndY=0 EndZ=0
  constraints (13):
    c: Vertical(g0)
    c: Distance(g0) = 1.5
    c: Horizontal(g1)
    c: Distance(g1) = 5
    c: Coincident(g1,g0)
    c: Vertical(g2)
    c: Distance(g2) = 1.5
    c: Coincident(g2,g1)
    c: Block(g1)
    c: Block(g2)
    c: Block(g0)
    c: Coincident(g3,g0)
    c: Coincident(g3,g2)
FEATURE [Part::Extrusion] Extrude022  label="solenoidDriverBottomLipTopExtrude014"
  Base = -> Sketch025
  Dir = (0,0.894389,-0.447291)
  DirMode = 2
  FaceMakerClass = Part::FaceMakerBullseye
  LengthFwd = -6.5
  LengthRev = 0
  Placement = pos=(0,-15.45,20.3) rot=(1,0,0;1.5708rad)
  Solid = true
  Symmetric = false
FEATURE [Part::Fillet] Fillet013  label="solenoidDriverBottomLipTopFillet006"
  Base = -> Extrude022
  Edges = 1 edges r=1.4: [Edge6]
  Placement = pos=(5,0,0) rot=(0,0,1;0rad)
FEATURE [Sketcher::SketchObject] Sketch026
  FullyConstrained = true
  Placement = pos=(0,-14.3,2.37) rot=(-1,0,0;2.03453rad)
  sketch-geometry (4):
    g0: LineSegment StartX=0 StartY=1.5 StartZ=0 EndX=0 EndY=0 EndZ=0
    g1: LineSegment StartX=0 StartY=1.5 StartZ=0 EndX=5 EndY=1.5 EndZ=0
    g2: LineSegment StartX=5 StartY=1.5 StartZ=0 EndX=5 EndY=0 EndZ=0
    g3: LineSegment StartX=0 StartY=0 StartZ=0 EndX=5 EndY=0 EndZ=0
  constraints (13):
    c: Vertical(g0)
    c: Distance(g0) = 1.5
    c: Horizontal(g1)
    c: Distance(g1) = 5
    c: Coincident(g1,g0)
    c: Vertical(g2)
    c: Distance(g2) = 1.5
    c: Coincident(g2,g1)
    c: Block(g1)
    c: Block(g2)
    c: Block(g0)
    c: Coincident(g3,g0)
    c: Coincident(g3,g2)
FEATURE [Part::Extrusion] Extrude023  label="solenoidDriverBottomLipTopExtrude015"
  Base = -> Sketch026
  Dir = (0,0.894389,-0.447291)
  DirMode = 2
  FaceMakerClass = Part::FaceMakerBullseye
  LengthFwd = -6.5
  LengthRev = 0
  Placement = pos=(5,-14.15,19.65) rot=(1,0,0;1.5708rad)
  Solid = true
  Symmetric = false
FEATURE [Sketcher::SketchObject] Sketch027
  FullyConstrained = true
  Placement = pos=(0,-14.3,2.37) rot=(-1,0,0;2.03453rad)
  sketch-geometry (5):
    g0: LineSegment StartX=45.5 StartY=-21.2 StartZ=0 EndX=49.5 EndY=-21.2 EndZ=0
    g1: LineSegment StartX=49.5 StartY=0 StartZ=0 EndX=49.5 EndY=-21.2 EndZ=0
    g2: LineSegment StartX=49.5 StartY=0 StartZ=0 EndX=49.5 EndY=1.6 EndZ=0
    g3: LineSegment StartX=45.5 StartY=-21.2 StartZ=0 EndX=45.5 EndY=1.6 EndZ=0
    g4: LineSegment StartX=49.5 StartY=1.6 StartZ=0 EndX=45.5 EndY=1.6 EndZ=0
  constraints (14):
    c: Horizontal(g0)
    c: Distance(g0) = 4
    c: Coincident(g1,g0)
    c: Vertical(g1)
    c: Block(g1)
    c: Vertical(g2)
    c: Distance(g2) = 1.6
    c: Block(g2)
    c: Coincident(g3,g0)
    c: Vertical(g3)
    c: Coincident(g4,g2)
    c: Horizontal(g4)
    c: Block(g0)
    c: Coincident(g3,g4)
FEATURE [Part::Extrusion] Extrude024
  Base = -> Sketch027
  Dir = (0,0.894389,-0.447291)
  DirMode = 2
  FaceMakerClass = Part::FaceMakerBullseye
  LengthFwd = 6.34
  LengthRev = 0
  Placement = pos=(0,-5.59,1) rot=(0,0,1;0rad)
  Solid = true
  Symmetric = false
FEATURE [Part::Fillet] Fillet014  label="solenoidDriverSideBarFillet014"
  Base = -> Extrude024
  Edges = 1 edges r=1.4: [Edge14]
  Placement = pos=(0,0.9,-0.45) rot=(0,0,1;0rad)
FEATURE [Part::Revolution] Revolve  label="mainScrewStandRevolve"
  Angle = 360
  Axis = (0,0,1)
  Base = (0,0,0)
  FaceMakerClass = Part::FaceMakerBullseye
  Placement = pos=(121.35,-15.3,0) rot=(0,0,1;0rad)
  Solid = true
  Source = -> Sketch004
  Symmetric = false
FEATURE [Part::Extrusion] Extrude021  label="solenoidDriverTopLipLowerExtrude011"
  Base = -> Sketch024
  Dir = (0,0.894389,-0.447291)
  DirMode = 2
  FaceMakerClass = Part::FaceMakerBullseye
  LengthFwd = 5.05
  LengthRev = 0
  Solid = true
  Symmetric = false
FEATURE [Part::Fillet] Fillet012  label="solenoidDriverTopLipLowerFillet004"
  Base = -> Extrude021
  Edges = 1 edges r=1.2: [Edge7]
  Placement = pos=(0,-0.9,-1.35) rot=(0,0,1;0rad)
FEATURE [Part::Fillet] Fillet003  label="solenoidDriverTopLipLowerFillet003"
  Base = -> Extrude010
  Edges = 1 edges r=1.2: [Edge7]
  Placement = pos=(0,-3,-0.3) rot=(0,0,1;0rad)
FEATURE [Part::Extrusion] Extrude025  label="mainBodyUpperExtrude025"
  Base = -> Sketch001
  Dir = (0,0,1)
  DirMode = 2
  FaceMakerClass = Part::FaceMakerBullseye
  LengthFwd = 20
  LengthRev = 0
  Solid = true
  Symmetric = false
FEATURE [Part::MultiFuse] Fusion  label="solenoidDriverBottomLipFusion"
  Placement = pos=(0,-1.6,0) rot=(0,0,1;0rad)
  Shapes = -> [Fillet005,Fillet013,Extrude023,Extrude013]
FEATURE [Sketcher::SketchObject] Sketch028
  FullyConstrained = true
  Placement = pos=(0,-14.3,2.37) rot=(-1,0,0;2.03453rad)
  sketch-geometry (4):
    g0: LineSegment StartX=0 StartY=1.5 StartZ=0 EndX=0 EndY=0 EndZ=0
    g1: LineSegment StartX=0 StartY=1.5 StartZ=0 EndX=5 EndY=1.5 EndZ=0
    g2: LineSegment StartX=5 StartY=1.5 StartZ=0 EndX=5 EndY=0 EndZ=0
    g3: LineSegment StartX=0 StartY=0 StartZ=0 EndX=5 EndY=0 EndZ=0
  constraints (13):
    c: Vertical(g0)
    c: Distance(g0) = 1.5
    c: Horizontal(g1)
    c: Distance(g1) = 5
    c: Coincident(g1,g0)
    c: Vertical(g2)
    c: Distance(g2) = 1.5
    c: Coincident(g2,g1)
    c: Block(g1)
    c: Block(g2)
    c: Block(g0)
    c: Coincident(g3,g0)
    c: Coincident(g3,g2)
FEATURE [Part::Extrusion] Extrude026  label="solenoidDriverBottomLipTopExtrude016"
  Base = -> Sketch028
  Dir = (0,0.894389,-0.447291)
  DirMode = 2
  FaceMakerClass = Part::FaceMakerBullseye
  LengthFwd = -6.5
  LengthRev = 0
  Placement = pos=(5,-14.15,19.65) rot=(1,0,0;1.5708rad)
  Solid = true
  Symmetric = false
FEATURE [Sketcher::SketchObject] Sketch029
  FullyConstrained = true
  Placement = pos=(0,-14.3,2.37) rot=(-1,0,0;2.03453rad)
  sketch-geometry (4):
    g0: LineSegment StartX=0 StartY=1.5 StartZ=0 EndX=0 EndY=0 EndZ=0
    g1: LineSegment StartX=0 StartY=1.5 StartZ=0 EndX=5 EndY=1.5 EndZ=0
    g2: LineSegment StartX=5 StartY=1.5 StartZ=0 EndX=5 EndY=0 EndZ=0
    g3: LineSegment StartX=0 StartY=0 StartZ=0 EndX=5 EndY=0 EndZ=0
  constraints (13):
    c: Vertical(g0)
    c: Distance(g0) = 1.5
    c: Horizontal(g1)
    c: Distance(g1) = 5
    c: Coincident(g1,g0)
    c: Vertical(g2)
    c: Distance(g2) = 1.5
    c: Coincident(g2,g1)
    c: Block(g1)
    c: Block(g2)
    c: Block(g0)
    c: Coincident(g3,g0)
    c: Coincident(g3,g2)
FEATURE [Part::Extrusion] Extrude027  label="solenoidDriverBottomLipTopExtrude017"
  Base = -> Sketch029
  Dir = (0,0.894389,-0.447291)
  DirMode = 2
  FaceMakerClass = Part::FaceMakerBullseye
  LengthFwd = -6.5
  LengthRev = 0
  Placement = pos=(0,-14.15,19.65) rot=(1,0,0;1.5708rad)
  Solid = true
  Symmetric = false
FEATURE [Sketcher::SketchObject] Sketch030
  FullyConstrained = true
  Placement = pos=(0,-14.3,2.37) rot=(-1,0,0;2.03453rad)
  sketch-geometry (4):
    g0: LineSegment StartX=0 StartY=1.5 StartZ=0 EndX=0 EndY=0 EndZ=0
    g1: LineSegment StartX=0 StartY=1.5 StartZ=0 EndX=5 EndY=1.5 EndZ=0
    g2: LineSegment StartX=5 StartY=1.5 StartZ=0 EndX=5 EndY=0 EndZ=0
    g3: LineSegment StartX=0 StartY=0 StartZ=0 EndX=5 EndY=0 EndZ=0
  constraints (13):
    c: Vertical(g0)
    c: Distance(g0) = 1.5
    c: Horizontal(g1)
    c: Distance(g1) = 5
    c: Coincident(g1,g0)
    c: Vertical(g2)
    c: Distance(g2) = 1.5
    c: Coincident(g2,g1)
    c: Block(g1)
    c: Block(g2)
    c: Block(g0)
    c: Coincident(g3,g0)
    c: Coincident(g3,g2)
FEATURE [Sketcher::SketchObject] Sketch031
  FullyConstrained = true
  Placement = pos=(0,-14.3,2.37) rot=(-1,0,0;2.03453rad)
  sketch-geometry (6):
    g0: LineSegment StartX=45.5 StartY=-21.2 StartZ=0 EndX=49.5 EndY=-21.2 EndZ=0
    g1: LineSegment StartX=45.5 StartY=0 StartZ=0 EndX=49.5 EndY=0 EndZ=0
    g2: LineSegment StartX=49.5 StartY=0 StartZ=0 EndX=49.5 EndY=-21.2 EndZ=0
    g3: LineSegment StartX=4 StartY=0 StartZ=0 EndX=4 EndY=-21.2 EndZ=0
    g4: LineSegment StartX=45.5 StartY=-21.2 StartZ=0 EndX=4 EndY=-21.2 EndZ=0
    g5: LineSegment StartX=4 StartY=0 StartZ=0 EndX=45.5 EndY=0 EndZ=0
  constraints (16):
    c: Horizontal(g0)
    c: Distance(g0) = 4
    c: Horizontal(g1)
    c: Distance(g1) = 4
    c: Coincident(g2,g1)
    c: Coincident(g2,g0)
    c: Vertical(g2)
    c: Block(g2)
    c: Vertical(g3)
    c: Coincident(g4,g0)
    c: Horizontal(g4)
    c: Coincident(g4,g3)
    c: Coincident(g5,g1)
    c: Horizontal(g5)
    c: Block(g3)
    c: Block(g5)
FEATURE [Part::Extrusion] Extrude028  label="removeFromSolenoidDriverMainExtrude021"
  Base = -> Sketch031
  Dir = (0,0.894389,-0.447291)
  DirMode = 2
  FaceMakerClass = Part::FaceMakerBullseye
  LengthFwd = 3.1
  LengthRev = 0
  Placement = pos=(-4,-2.42,-0.8) rot=(0,0,1;0rad)
  Solid = true
  Symmetric = false
FEATURE [Part::Extrusion] Extrude029  label="solenoidDriverBottomLipTopExtrude018"
  Base = -> Sketch030
  Dir = (0,0.894389,-0.447291)
  DirMode = 2
  FaceMakerClass = Part::FaceMakerBullseye
  LengthFwd = -6.5
  LengthRev = 0
  Placement = pos=(5,-14.15,19.65) rot=(1,0,0;1.5708rad)
  Solid = true
  Symmetric = false
FEATURE [Sketcher::SketchObject] Sketch032
  FullyConstrained = true
  Placement = pos=(0,-14.3,2.37) rot=(-1,0,0;2.03453rad)
  sketch-geometry (4):
    g0: LineSegment StartX=0 StartY=1.5 StartZ=0 EndX=0 EndY=0 EndZ=0
    g1: LineSegment StartX=0 StartY=1.5 StartZ=0 EndX=5 EndY=1.5 EndZ=0
    g2: LineSegment StartX=5 StartY=1.5 StartZ=0 EndX=5 EndY=0 EndZ=0
    g3: LineSegment StartX=0 StartY=0 StartZ=0 EndX=5 EndY=0 EndZ=0
  constraints (13):
    c: Vertical(g0)
    c: Distance(g0) = 1.5
    c: Horizontal(g1)
    c: Distance(g1) = 5
    c: Coincident(g1,g0)
    c: Vertical(g2)
    c: Distance(g2) = 1.5
    c: Coincident(g2,g1)
    c: Block(g1)
    c: Block(g2)
    c: Block(g0)
    c: Coincident(g3,g0)
    c: Coincident(g3,g2)
FEATURE [Part::Extrusion] Extrude030  label="solenoidDriverBottomLipTopExtrude019"
  Base = -> Sketch032
  Dir = (0,0.894389,-0.447291)
  DirMode = 2
  FaceMakerClass = Part::FaceMakerBullseye
  LengthFwd = -6.5
  LengthRev = 0
  Placement = pos=(0,-14.15,19.65) rot=(1,0,0;1.5708rad)
  Solid = true
  Symmetric = false
FEATURE [Part::MultiFuse] Fusion004
  Placement = pos=(0,1.4,2.65) rot=(0,0,1;0rad)
  Shapes = -> [Extrude029,Extrude030]
FEATURE [Part::MultiFuse] Fusion003
  Placement = pos=(-2.3,0,0) rot=(0,0,1;0rad)
  Shapes = -> [Extrude028,Fusion004]
FEATURE [Sketcher::SketchObject] Sketch033
  FullyConstrained = true
  Placement = pos=(0,-14.3,2.37) rot=(-1,0,0;2.03453rad)
  sketch-geometry (4):
    g0: LineSegment StartX=0 StartY=1.5 StartZ=0 EndX=0 EndY=0 EndZ=0
    g1: LineSegment StartX=0 StartY=1.5 StartZ=0 EndX=5 EndY=1.5 EndZ=0
    g2: LineSegment StartX=5 StartY=1.5 StartZ=0 EndX=5 EndY=0 EndZ=0
    g3: LineSegment StartX=0 StartY=0 StartZ=0 EndX=5 EndY=0 EndZ=0
  constraints (13):
    c: Vertical(g0)
    c: Distance(g0) = 1.5
    c: Horizontal(g1)
    c: Distance(g1) = 5
    c: Coincident(g1,g0)
    c: Vertical(g2)
    c: Distance(g2) = 1.5
    c: Coincident(g2,g1)
    c: Block(g1)
    c: Block(g2)
    c: Block(g0)
    c: Coincident(g3,g0)
    c: Coincident(g3,g2)
FEATURE [Sketcher::SketchObject] Sketch034
  FullyConstrained = true
  Placement = pos=(0,-14.3,2.37) rot=(-1,0,0;2.03453rad)
  sketch-geometry (4):
    g0: LineSegment StartX=0 StartY=1.5 StartZ=0 EndX=0 EndY=0 EndZ=0
    g1: LineSegment StartX=0 StartY=1.5 StartZ=0 EndX=5 EndY=1.5 EndZ=0
    g2: LineSegment StartX=5 StartY=1.5 StartZ=0 EndX=5 EndY=0 EndZ=0
    g3: LineSegment StartX=0 StartY=0 StartZ=0 EndX=5 EndY=0 EndZ=0
  constraints (13):
    c: Vertical(g0)
    c: Distance(g0) = 1.5
    c: Horizontal(g1)
    c: Distance(g1) = 5
    c: Coincident(g1,g0)
    c: Vertical(g2)
    c: Distance(g2) = 1.5
    c: Coincident(g2,g1)
    c: Block(g1)
    c: Block(g2)
    c: Block(g0)
    c: Coincident(g3,g0)
    c: Coincident(g3,g2)
FEATURE [Part::Extrusion] Extrude020  label="removeFromSolenoidDriverMainExtrude020"
  Base = -> Sketch020
  Dir = (0,0.894389,-0.447291)
  DirMode = 2
  FaceMakerClass = Part::FaceMakerBullseye
  LengthFwd = 3.1
  LengthRev = 0
  Placement = pos=(-4,-2.42,-0.8) rot=(0,0,1;0rad)
  Solid = true
  Symmetric = false
FEATURE [Part::Fillet] Fillet
  Base = -> Fusion003
  Edges = 1 edges r=10: [Edge5]
  Placement = pos=(-2,0,0) rot=(0,0,1;0rad)
FEATURE [Part::MultiFuse] Fusion001
  Placement = pos=(0,1.4,2.65) rot=(0,0,1;0rad)
  Shapes = -> [Extrude026,Extrude027]
FEATURE [Part::MultiFuse] Fusion002
  Shapes = -> [Extrude020,Fusion001]
FEATURE [Sketcher::SketchObject] Sketch035
  FullyConstrained = true
  Placement = pos=(0,-14.3,2.37) rot=(-1,0,0;2.03453rad)
  sketch-geometry (4):
    g0: LineSegment StartX=0 StartY=1.5 StartZ=0 EndX=0 EndY=0 EndZ=0
    g1: LineSegment StartX=0 StartY=1.5 StartZ=0 EndX=5 EndY=1.5 EndZ=0
    g2: LineSegment StartX=5 StartY=1.5 StartZ=0 EndX=5 EndY=0 EndZ=0
    g3: LineSegment StartX=0 StartY=0 StartZ=0 EndX=5 EndY=0 EndZ=0
  constraints (13):
    c: Vertical(g0)
    c: Distance(g0) = 1.5
    c: Horizontal(g1)
    c: Distance(g1) = 5
    c: Coincident(g1,g0)
    c: Vertical(g2)
    c: Distance(g2) = 1.5
    c: Coincident(g2,g1)
    c: Block(g1)
    c: Block(g2)
    c: Block(g0)
    c: Coincident(g3,g0)
    c: Coincident(g3,g2)
FEATURE [Sketcher::SketchObject] Sketch036
  FullyConstrained = true
  Placement = pos=(0,-14.3,2.37) rot=(-1,0,0;2.03453rad)
  sketch-geometry (4):
    g0: LineSegment StartX=0 StartY=1.5 StartZ=0 EndX=0 EndY=0 EndZ=0
    g1: LineSegment StartX=0 StartY=1.5 StartZ=0 EndX=5 EndY=1.5 EndZ=0
    g2: LineSegment StartX=5 StartY=1.5 StartZ=0 EndX=5 EndY=0 EndZ=0
    g3: LineSegment StartX=0 StartY=0 StartZ=0 EndX=5 EndY=0 EndZ=0
  constraints (13):
    c: Vertical(g0)
    c: Distance(g0) = 1.5
    c: Horizontal(g1)
    c: Distance(g1) = 5
    c: Coincident(g1,g0)
    c: Vertical(g2)
    c: Distance(g2) = 1.5
    c: Coincident(g2,g1)
    c: Block(g1)
    c: Block(g2)
    c: Block(g0)
    c: Coincident(g3,g0)
    c: Coincident(g3,g2)
FEATURE [Part::Extrusion] Extrude031  label="solenoidDriverBottomLipTopExtrude020"
  Base = -> Sketch035
  Dir = (0,0.894389,-0.447291)
  DirMode = 2
  FaceMakerClass = Part::FaceMakerBullseye
  LengthFwd = -6.5
  LengthRev = 0
  Placement = pos=(5,-14.15,19.65) rot=(1,0,0;1.5708rad)
  Solid = true
  Symmetric = false
FEATURE [Part::Extrusion] Extrude032  label="solenoidDriverBottomLipTopExtrude021"
  Base = -> Sketch036
  Dir = (0,0.894389,-0.447291)
  DirMode = 2
  FaceMakerClass = Part::FaceMakerBullseye
  LengthFwd = -6.5
  LengthRev = 0
  Placement = pos=(0,-14.15,19.65) rot=(1,0,0;1.5708rad)
  Solid = true
  Symmetric = false
FEATURE [Part::MultiFuse] Fusion009
  Placement = pos=(8,1.4,2.65) rot=(0,0,1;0rad)
  Shapes = -> [Extrude031,Extrude032]
FEATURE [Part::MultiFuse] Fusion010  label="removeFromSolenoidDriver"
  Shapes = -> [Fusion009,Fillet,Fusion002]
FEATURE [Sketcher::SketchObject] Sketch037
  FullyConstrained = true
  Placement = pos=(0,0,0) rot=(1,0,0;1.5708rad)
  sketch-geometry (4):
    g0: Circle CenterX=64.05 CenterY=16.5 CenterZ=0 NormalX=0 NormalY=0 NormalZ=1 AngleXU=0 Radius=2.7
    g1: Circle CenterX=64.05 CenterY=8.5 CenterZ=0 NormalX=0 NormalY=0 NormalZ=1 AngleXU=0 Radius=2.7
    g2: Circle CenterX=84.15 CenterY=8.5 CenterZ=0 NormalX=0 NormalY=0 NormalZ=1 AngleXU=0 Radius=2.7
    g3: Circle CenterX=84.15 CenterY=16.5 CenterZ=0 NormalX=0 NormalY=0 NormalZ=1 AngleXU=0 Radius=2.7
  constraints (4):
    c: Block(g2)
    c: Block(g3)
    c: Block(g0)
    c: Block(g1)
FEATURE [Part::Extrusion] Extrude033  label="removeFromMainBodyToCreateScrewHoleCounterSinks001"
  Base = -> Sketch037
  Dir = (0,-1,1.1e-15)
  DirMode = 2
  FaceMakerClass = Part::FaceMakerBullseye
  LengthFwd = 1.9
  LengthRev = 0
  Placement = pos=(0.8,0,0) rot=(0,0,1;0rad)
  Solid = true
  Symmetric = false
FEATURE [Part::MultiFuse] Fusion011  label="removeFromMainBodyToCreateScrewHoleCounterSinks001Fusion011"
  Shapes = -> [Extrude014,Extrude033]
FEATURE [Sketcher::SketchObject] Sketch038
  FullyConstrained = true
  Placement = pos=(0,-14.3,2.37) rot=(-1,0,0;2.03453rad)
  sketch-geometry (4):
    g0: LineSegment StartX=33.9 StartY=-9.7 StartZ=0 EndX=33.9 EndY=-1.5 EndZ=0
    g1: LineSegment StartX=33.9 StartY=-1.5 StartZ=0 EndX=44.5 EndY=-1.5 EndZ=0
    g2: LineSegment StartX=33.9 StartY=-9.7 StartZ=0 EndX=44.5 EndY=-9.7 EndZ=0
    g3: LineSegment StartX=44.5 StartY=-1.5 StartZ=0 EndX=44.5 EndY=-9.7 EndZ=0
  constraints (10):
    c: Vertical(g0)
    c: Coincident(g1,g0)
    c: Horizontal(g1)
    c: Block(g1)
    c: Block(g0)
    c: Coincident(g2,g0)
    c: Horizontal(g2)
    c: Coincident(g3,g1)
    c: Coincident(g3,g2)
    c: Vertical(g3)
FEATURE [Part::Extrusion] Extrude034
  Base = -> Sketch038
  Dir = (0,0.894389,-0.447291)
  DirMode = 2
  FaceMakerClass = Part::FaceMakerBullseye
  LengthFwd = 16
  LengthRev = 0
  Placement = pos=(0,-22,7) rot=(0,0,1;0rad)
  Solid = true
  Symmetric = false
FEATURE [Sketcher::SketchObject] Sketch039
  FullyConstrained = true
  Placement = pos=(0,-14.3,2.37) rot=(-1,0,0;2.03453rad)
  sketch-geometry (4):
    g0: LineSegment StartX=5.5 StartY=-7.7 StartZ=0 EndX=13.3 EndY=-7.7 EndZ=0
    g1: LineSegment StartX=13.3 StartY=-7.7 StartZ=0 EndX=13.3 EndY=-13.1 EndZ=0
    g2: LineSegment StartX=13.3 StartY=-13.1 StartZ=0 EndX=5.5 EndY=-13.1 EndZ=0
    g3: LineSegment StartX=5.5 StartY=-7.7 StartZ=0 EndX=5.5 EndY=-13.1 EndZ=0
  constraints (12):
    c: Horizontal(g0)
    c: Distance(g0) = 7.8
    c: Coincident(g1,g0)
    c: Vertical(g1)
    c: Distance(g1) = 5.4
    c: Coincident(g2,g1)
    c: Horizontal(g2)
    c: Vertical(g3)
    c: Coincident(g3,g2)
    c: Block(g0)
    c: Block(g2)
    c: Block(g3)
FEATURE [Part::Extrusion] Extrude035  label="removeToMakeHoleForConnectorExtrude035"
  Base = -> Sketch039
  Dir = (0,0.894389,-0.447291)
  DirMode = 2
  FaceMakerClass = Part::FaceMakerBullseye
  LengthFwd = 15
  LengthRev = 0
  Placement = pos=(-4,-22,9.6469) rot=(0,0,1;0rad)
  Solid = true
  Symmetric = false
FEATURE [App::MeasureDistance] Distance  label="Distance: 4.00 mm"
  Distance = 4.00184
  P1 = (119.349,-15.3,8)
  P2 = (123.351,-15.3,8)
FEATURE [App::MeasureDistance] Distance001  label="Distance: 3.80 mm"
  Distance = 3.8
  P1 = (119.45,-15.3,8)
  P2 = (123.25,-15.3,8)
FEATURE [Part::Fillet] Fillet015
  Base = -> Extrude009
  Edges = 1 edges r=1.59: [Edge7]
FEATURE [Part::Fillet] Fillet016
  Base = -> Extrude017
  Edges = 1 edges r=1.49: [Edge12]
FEATURE [Part::Fillet] Fillet017
  Base = -> Fillet016
  Edges = 1 edges r=1.45: [Edge8]
FEATURE [Part::MultiFuse] Fusion012  label="main"
  Shapes = -> [Extrude,Revolve,Extrude005,Fillet003,Fillet012,Fillet014,Extrude025,Fusion,Fillet015,Fillet017]
FEATURE [Part::Cut] Cut001
  Base = -> Fusion012
  Tool = -> Box003
FEATURE [Part::Cut] Cut002
  Base = -> Cut001
  Tool = -> Box002
FEATURE [Part::Cut] Cut003
  Base = -> Cut002
  Tool = -> Cut
FEATURE [Part::Cut] Cut004
  Base = -> Cut003
  Tool = -> Extrude019
FEATURE [Part::Cut] Cut005
  Base = -> Cut004
  Tool = -> Fusion011
FEATURE [Part::Cut] Cut006
  Base = -> Cut005
  Tool = -> Extrude004
FEATURE [Part::Cut] Cut007
  Base = -> Cut006
  Tool = -> Extrude015
FEATURE [Part::Cut] Cut008
  Base = -> Cut007
  Tool = -> Extrude008
FEATURE [Part::Cut] Cut009
  Base = -> Cut008
  Tool = -> Fusion010
FEATURE [App::MeasureDistance] Distance002  label="Distance: 2.05 mm"
  Distance = 2.05453
  P1 = (1.5,-23.0732,21.402)
  P2 = (6e-15,-23,20)
FEATURE [Part::Cut] Cut010
  Base = -> Cut009
  Tool = -> Extrude035
FEATURE [Part::Cut] Cut011
  Base = -> Cut010
  Tool = -> Extrude034
FEATURE [Part::Box] Box004  label="Cube004"
  AttacherType = Attacher::AttachEngine3D
  Height = 10
  Length = 200
  Placement = pos=(-30,0,0) rot=(0,0,1;0rad)
  Width = 10
FEATURE [Part::Fillet] Fillet020
  Base = -> Box004
  Edges = 1 edges r=3.6: [Edge12]
FEATURE [Part::Box] Box005  label="Cube005"
  AttacherType = Attacher::AttachEngine3D
  Height = 10
  Length = 198
  Placement = pos=(-30,0,0) rot=(0,0,1;0rad)
  Width = 10
FEATURE [Part::Cut] Cut012
  Base = -> Box005
  Tool = -> Fillet020
FEATURE [Part::Box] Box006  label="Cube006"
  AttacherType = Attacher::AttachEngine3D
  Height = 5
  Length = 200
  Placement = pos=(-30,6.4,10) rot=(1,0,0;0rad)
  Width = 5
FEATURE [Part::Box] Box007  label="Cube007"
  AttacherType = Attacher::AttachEngine3D
  Height = 5
  Length = 200
  Placement = pos=(-30,6.4,10) rot=(1,0,0;0.872665rad)
  Width = 5
FEATURE [Part::MultiFuse] Fusion013  label="removeFromMainFusion013"
  Placement = pos=(0,-10,10) rot=(0,0,1;0rad)
  Shapes = -> [Box007,Box006,Cut012]
FEATURE [Mesh::Feature] v0_98_Cut013  label="v0_98-Cut013"
FEATURE [App::MeasureDistance] Distance003  label="Distance: 7.18 mm"
  Distance = 7.17719
  P1 = (117.773,-15.3145,-2.4)
  P2 = (124.951,-15.2973,-2.4)
FEATURE [Sketcher::SketchObject] Sketch040
  FullyConstrained = true
  Placement = pos=(0,-14.3,2.37) rot=(-1,0,0;2.03453rad)
  sketch-geometry (4):
    g0: LineSegment StartX=0 StartY=1.5 StartZ=0 EndX=0 EndY=0 EndZ=0
    g1: LineSegment StartX=0 StartY=1.5 StartZ=0 EndX=5 EndY=1.5 EndZ=0
    g2: LineSegment StartX=5 StartY=1.5 StartZ=0 EndX=5 EndY=0 EndZ=0
    g3: LineSegment StartX=0 StartY=0 StartZ=0 EndX=5 EndY=0 EndZ=0
  constraints (13):
    c: Vertical(g0)
    c: Distance(g0) = 1.5
    c: Horizontal(g1)
    c: Distance(g1) = 5
    c: Coincident(g1,g0)
    c: Vertical(g2)
    c: Distance(g2) = 1.5
    c: Coincident(g2,g1)
    c: Block(g1)
    c: Block(g2)
    c: Block(g0)
    c: Coincident(g3,g0)
    c: Coincident(g3,g2)
FEATURE [Part::Extrusion] Extrude036
  Base = -> Sketch040
  Dir = (0,0.894389,-0.447291)
  DirMode = 2
  FaceMakerClass = Part::FaceMakerBullseye
  LengthFwd = 1.4
  LengthRev = 0
  Placement = pos=(0,8.25,17.58) rot=(0,0,1;0rad)
  Solid = true
  Symmetric = false
FEATURE [Sketcher::SketchObject] Sketch041
  FullyConstrained = true
  Placement = pos=(0,-14.3,2.37) rot=(-1,0,0;2.03453rad)
  sketch-geometry (4):
    g0: LineSegment StartX=0 StartY=1.5 StartZ=0 EndX=0 EndY=0 EndZ=0
    g1: LineSegment StartX=0 StartY=1.5 StartZ=0 EndX=5 EndY=1.5 EndZ=0
    g2: LineSegment StartX=5 StartY=1.5 StartZ=0 EndX=5 EndY=0 EndZ=0
    g3: LineSegment StartX=0 StartY=0 StartZ=0 EndX=5 EndY=0 EndZ=0
  constraints (13):
    c: Vertical(g0)
    c: Distance(g0) = 1.5
    c: Horizontal(g1)
    c: Distance(g1) = 5
    c: Coincident(g1,g0)
    c: Vertical(g2)
    c: Distance(g2) = 1.5
    c: Coincident(g2,g1)
    c: Block(g1)
    c: Block(g2)
    c: Block(g0)
    c: Coincident(g3,g0)
    c: Coincident(g3,g2)
FEATURE [Part::Extrusion] Extrude037
  Base = -> Sketch041
  Dir = (0,0.894389,-0.447291)
  DirMode = 2
  FaceMakerClass = Part::FaceMakerBullseye
  LengthFwd = 1.4
  LengthRev = 0
  Placement = pos=(0,6.11,13.33) rot=(0,0,1;0rad)
  Solid = true
  Symmetric = false
FEATURE [Part::MultiFuse] Fusion014  label="screwSpacerFusion014"
  Shapes = -> [Extrude037,Extrude036]
FEATURE [Sketcher::SketchObject] Sketch042
  FullyConstrained = true
  Placement = pos=(0,-14.3,2.37) rot=(-1,0,0;2.03453rad)
  sketch-geometry (4):
    g0: LineSegment StartX=0 StartY=1.5 StartZ=0 EndX=0 EndY=0 EndZ=0
    g1: LineSegment StartX=0 StartY=1.5 StartZ=0 EndX=5 EndY=1.5 EndZ=0
    g2: LineSegment StartX=5 StartY=1.5 StartZ=0 EndX=5 EndY=0 EndZ=0
    g3: LineSegment StartX=0 StartY=0 StartZ=0 EndX=5 EndY=0 EndZ=0
  constraints (13):
    c: Vertical(g0)
    c: Distance(g0) = 1.5
    c: Horizontal(g1)
    c: Distance(g1) = 5
    c: Coincident(g1,g0)
    c: Vertical(g2)
    c: Distance(g2) = 1.5
    c: Coincident(g2,g1)
    c: Block(g1)
    c: Block(g2)
    c: Block(g0)
    c: Coincident(g3,g0)
    c: Coincident(g3,g2)
FEATURE [Part::Extrusion] Extrude038
  Base = -> Sketch042
  Dir = (0,0.894389,-0.447291)
  DirMode = 2
  FaceMakerClass = Part::FaceMakerBullseye
  LengthFwd = 1.4
  LengthRev = 0
  Placement = pos=(0,8.459,18) rot=(0,0,1;0rad)
  Solid = true
  Symmetric = false
FEATURE [Part::MultiFuse] Fusion015  label="screwSpacerFusion014Fusion015"
  Placement = pos=(0,0.35,-0.18) rot=(0,0,1;0rad)
  Shapes = -> [Extrude038,Fusion014]
FEATURE [Part::Cylinder] Cylinder
  Angle = 360
  AttacherType = Attacher::AttachEngine3D
  Height = 10
  Placement = pos=(0,10,0) rot=(0,0,1;0rad)
  Radius = 1.5
FEATURE [Part::Cylinder] Cylinder001
  Angle = 360
  AttacherType = Attacher::AttachEngine3D
  Height = 10
  Placement = pos=(3,10,0) rot=(0,0,1;0rad)
  Radius = 1.5
FEATURE [Part::Box] Box008  label="Cube008"
  AttacherType = Attacher::AttachEngine3D
  Height = 10
  Length = 3
  Placement = pos=(0,8.5,0) rot=(0,0,1;0rad)
  Width = 3
FEATURE [Part::MultiFuse] Fusion016  label="holeForWireFusion016"
  Shapes = -> [Cylinder001,Box008,Cylinder]
FEATURE [Part::Box] Box009  label="Cube009"
  AttacherType = Attacher::AttachEngine3D
  Height = 10
  Length = 3
  Placement = pos=(0,8.5,0) rot=(0,0,1;0rad)
  Width = 3
FEATURE [Part::Cylinder] Cylinder002
  Angle = 360
  AttacherType = Attacher::AttachEngine3D
  Height = 10
  Placement = pos=(0,10,0) rot=(0,0,1;0rad)
  Radius = 1.5
FEATURE [Part::Cylinder] Cylinder003
  Angle = 360
  AttacherType = Attacher::AttachEngine3D
  Height = 10
  Placement = pos=(3,10,0) rot=(0,0,1;0rad)
  Radius = 1.5
FEATURE [Part::MultiFuse] Fusion017  label="holeForWireFusion017"
  Placement = pos=(0,0,10) rot=(0,0,1;0rad)
  Shapes = -> [Cylinder003,Box009,Cylinder002]
FEATURE [Part::MultiFuse] Fusion018  label="holeForWireFusion018"
  Placement = pos=(0,0,0) rot=(0,1,0;-1.5708rad)
  Shapes = -> [Fusion017,Fusion016]
FEATURE [Part::Box] Box010  label="Cube010"
  AttacherType = Attacher::AttachEngine3D
  Height = 0.1
  Length = 0.1
  Placement = pos=(-2,10,0) rot=(0,0.995037,0.099504;0rad)
  Width = 0.1
FEATURE [Part::MultiFuse] Fusion019
  Placement = pos=(0,10,0) rot=(1,0,0;1.5708rad)
  Shapes = -> [Box010,Fusion018]
FEATURE [Part::Box] Box011  label="Cube011"
  AttacherType = Attacher::AttachEngine3D
  Height = 0.1
  Length = 1.1
  Placement = pos=(-2,10,10) rot=(0,0.995037,0.099504;0rad)
  Width = 0.1
FEATURE [Part::MultiFuse] Fusion020
  Placement = pos=(0,0,0) rot=(0,1,0;0.349066rad)
  Shapes = -> [Box011,Fusion019]
FEATURE [Part::Box] Box012  label="Cube012"
  AttacherType = Attacher::AttachEngine3D
  Height = 0.1
  Length = 1.1
  Placement = pos=(-2,10,10) rot=(0,0.995037,0.099504;0rad)
  Width = 0.1
FEATURE [Part::MultiFuse] Fusion021
  Placement = pos=(0,30,0) rot=(0,0,1;-2.6529rad)
  Shapes = -> [Box012,Fusion020]
FEATURE [Part::Box] Box013  label="Cube013"
  AttacherType = Attacher::AttachEngine3D
  Height = 0.1
  Length = 1.1
  Placement = pos=(2,19,10) rot=(0,0.995037,0.099504;0rad)
  Width = 0.1
FEATURE [Part::MultiFuse] Fusion022  label="holeForWire"
  Placement = pos=(15,-49.8,-8.2) rot=(0,0,1;0rad)
  Shapes = -> [Box013,Fusion021]
FEATURE [Part::Cut] Cut013
  Base = -> Cut011
  Tool = -> Fusion013
FEATURE [Part::Cut] Cut014
  Base = -> Cut013
  Tool = -> Fusion022
FEATURE [Sketcher::SketchObject] Sketch043
  FullyConstrained = true
  MapMode = 4
  Placement = pos=(0,0,0) rot=(0.57735,0.57735,0.57735;2.0944rad)
  Support = -> [Cut014]
  sketch-geometry (14):
    g0: LineSegment StartX=6.08745 StartY=-4.11588 StartZ=0 EndX=6.08745 EndY=-2.11589 EndZ=0
    g1: LineSegment StartX=3.58745 StartY=2.38411 StartZ=0 EndX=3.58745 EndY=4.38411 EndZ=0
    g2: LineSegment StartX=8.08745 StartY=1.38411 StartZ=0 EndX=8.08745 EndY=-1.11589 EndZ=0
    g3: ArcOfCircle CenterX=7.08745 CenterY=-1.11589 CenterZ=0 NormalX=0 NormalY=0 NormalZ=1 AngleXU=0 Radius=1 StartAngle=4.71239 EndAngle=6.28319
    g4: LineSegment StartX=6.08745 StartY=-2.11589 StartZ=0 EndX=7.08745 EndY=-2.11589 EndZ=0
    g5: LineSegment StartX=6.08745 StartY=-4.11588 StartZ=0 EndX=7.08745 EndY=-4.11588 EndZ=0
    g6: ArcOfCircle CenterX=7.08745 CenterY=-1.11589 CenterZ=0 NormalX=0 NormalY=0 NormalZ=1 AngleXU=0 Radius=3 StartAngle=4.71239 EndAngle=6.28319
    g7: ArcOfCircle CenterX=7.08745 CenterY=1.38411 CenterZ=0 NormalX=0 NormalY=0 NormalZ=1 AngleXU=0 Radius=1 StartAngle=5.35e-14 EndAngle=1.5708
    g8: LineSegment StartX=3.58745 StartY=4.38411 StartZ=0 EndX=7.08745 EndY=4.38411 EndZ=0
    g9: LineSegment StartX=10.0875 StartY=-1.11588 StartZ=0 EndX=10.0875 EndY=1.38411 EndZ=0
    g10: ArcOfCircle CenterX=7.08745 CenterY=1.38411 CenterZ=0 NormalX=0 NormalY=0 NormalZ=1 AngleXU=0 Radius=3 StartAngle=3.57e-14 EndAngle=1.5708
    g11: LineSegment StartX=3.58745 StartY=2.38411 StartZ=0 EndX=3.58745 EndY=1.38411 EndZ=0
    g12: ArcOfCircle CenterX=4.58745 CenterY=1.38412 CenterZ=0 NormalX=0 NormalY=0 NormalZ=1 AngleXU=0 Radius=1 StartAngle=1.57081 EndAngle=3.14159
    g13: LineSegment StartX=4.58744 StartY=2.38411 StartZ=0 EndX=7.08745 EndY=2.38411 EndZ=0
  constraints (33):
    c: Vertical(g0)
    c: Vertical(g1)
    c: Distance(g1) = 2
    c: Block(g0)
    c: Block(g2)
    c: Coincident(g3,g2)
    c: Coincident(g4,g0)
    c: Coincident(g4,g3)
    c: Horizontal(g4)
    c: Block(g3)
    c: Coincident(g5,g0)
    c: Horizontal(g5)
    c: Coincident(g6,g3)
    c: Block(g6)
    c: Block(g5)
    c: Coincident(g7,g2)
    c: Block(g7)
    c: Coincident(g8,g1)
    c: Coincident(g9,g6)
    c: Vertical(g9)
    c: Coincident(g10,g7)
    c: Block(g10)
    c: Block(g8)
    c: Block(g9)
    c: Coincident(g11,g1)
    c: Vertical(g11)
    c: Distance(g11) = 1
    c: Coincident(g12,g11)
    c: Coincident(g13,g12)
    c: Coincident(g13,g7)
    c: Horizontal(g13)
    c: Block(g13)
    c: Block(g12)
FEATURE [Sketcher::SketchObject] Sketch044
  FullyConstrained = true
  MapMode = 4
  Placement = pos=(0,0,0) rot=(0.57735,0.57735,0.57735;2.0944rad)
  Support = -> [Cut014]
  sketch-geometry (14):
    g0: LineSegment StartX=6.08745 StartY=-4.11588 StartZ=0 EndX=6.08745 EndY=-2.11589 EndZ=0
    g1: LineSegment StartX=8.08745 StartY=1.38411 StartZ=0 EndX=8.08745 EndY=-1.11589 EndZ=0
    g2: ArcOfCircle CenterX=7.08745 CenterY=-1.11589 CenterZ=0 NormalX=0 NormalY=0 NormalZ=1 AngleXU=0 Radius=1 StartAngle=4.71239 EndAngle=6.28319
    g3: LineSegment StartX=6.08745 StartY=-2.11589 StartZ=0 EndX=7.08745 EndY=-2.11589 EndZ=0
    g4: LineSegment StartX=6.08745 StartY=-4.11588 StartZ=0 EndX=7.08745 EndY=-4.11588 EndZ=0
    g5: ArcOfCircle CenterX=7.08745 CenterY=-1.11589 CenterZ=0 NormalX=0 NormalY=0 NormalZ=1 AngleXU=0 Radius=3 StartAngle=4.71239 EndAngle=6.28319
    g6: ArcOfCircle CenterX=7.08745 CenterY=1.38411 CenterZ=0 NormalX=0 NormalY=0 NormalZ=1 AngleXU=0 Radius=1 StartAngle=5.35e-14 EndAngle=1.5708
    g7: LineSegment StartX=10.0875 StartY=-1.11588 StartZ=0 EndX=10.0875 EndY=1.38411 EndZ=0
    g8: ArcOfCircle CenterX=7.08745 CenterY=1.38411 CenterZ=0 NormalX=0 NormalY=0 NormalZ=1 AngleXU=0 Radius=3 StartAngle=3.57e-14 EndAngle=1.5708
    g9: ArcOfCircle CenterX=4.58745 CenterY=1.38412 CenterZ=0 NormalX=0 NormalY=0 NormalZ=1 AngleXU=0 Radius=1 StartAngle=1.57081 EndAngle=3.14159
    g10: LineSegment StartX=4.58744 StartY=2.38411 StartZ=0 EndX=7.08745 EndY=2.38411 EndZ=0
    g11: LineSegment StartX=4.58745 StartY=4.38411 StartZ=0 EndX=7.08745 EndY=4.38411 EndZ=0
    g12: ArcOfCircle CenterX=4.58745 CenterY=5.38411 CenterZ=0 NormalX=0 NormalY=0 NormalZ=1 AngleXU=0 Radius=1 StartAngle=3.14159 EndAngle=4.71239
    g13: LineSegment StartX=3.58745 StartY=5.38411 StartZ=0 EndX=3.58745 EndY=1.38411 EndZ=0
  constraints (33):
    c: Vertical(g0)
    c: Block(g0)
    c: Block(g1)
    c: Coincident(g2,g1)
    c: Coincident(g3,g0)
    c: Coincident(g3,g2)
    c: Horizontal(g3)
    c: Block(g2)
    c: Coincident(g4,g0)
    c: Horizontal(g4)
    c: Coincident(g5,g2)
    c: Block(g5)
    c: Block(g4)
    c: Coincident(g6,g1)
    c: Block(g6)
    c: Coincident(g7,g5)
    c: Vertical(g7)
    c: Coincident(g8,g6)
    c: Block(g8)
    c: Block(g7)
    c: Coincident(g10,g9)
    c: Coincident(g10,g6)
    c: Horizontal(g10)
    c: Block(g10)
    c: Block(g9)
    c: Coincident(g11,g8)
    c: Horizontal(g11)
    c: Block(g12)
    c: Block(g11)
    c: Coincident(g13,g12)
    c: Coincident(g13,g9)
    c: Vertical(g13)
    c: Tangent(g13,g9)
